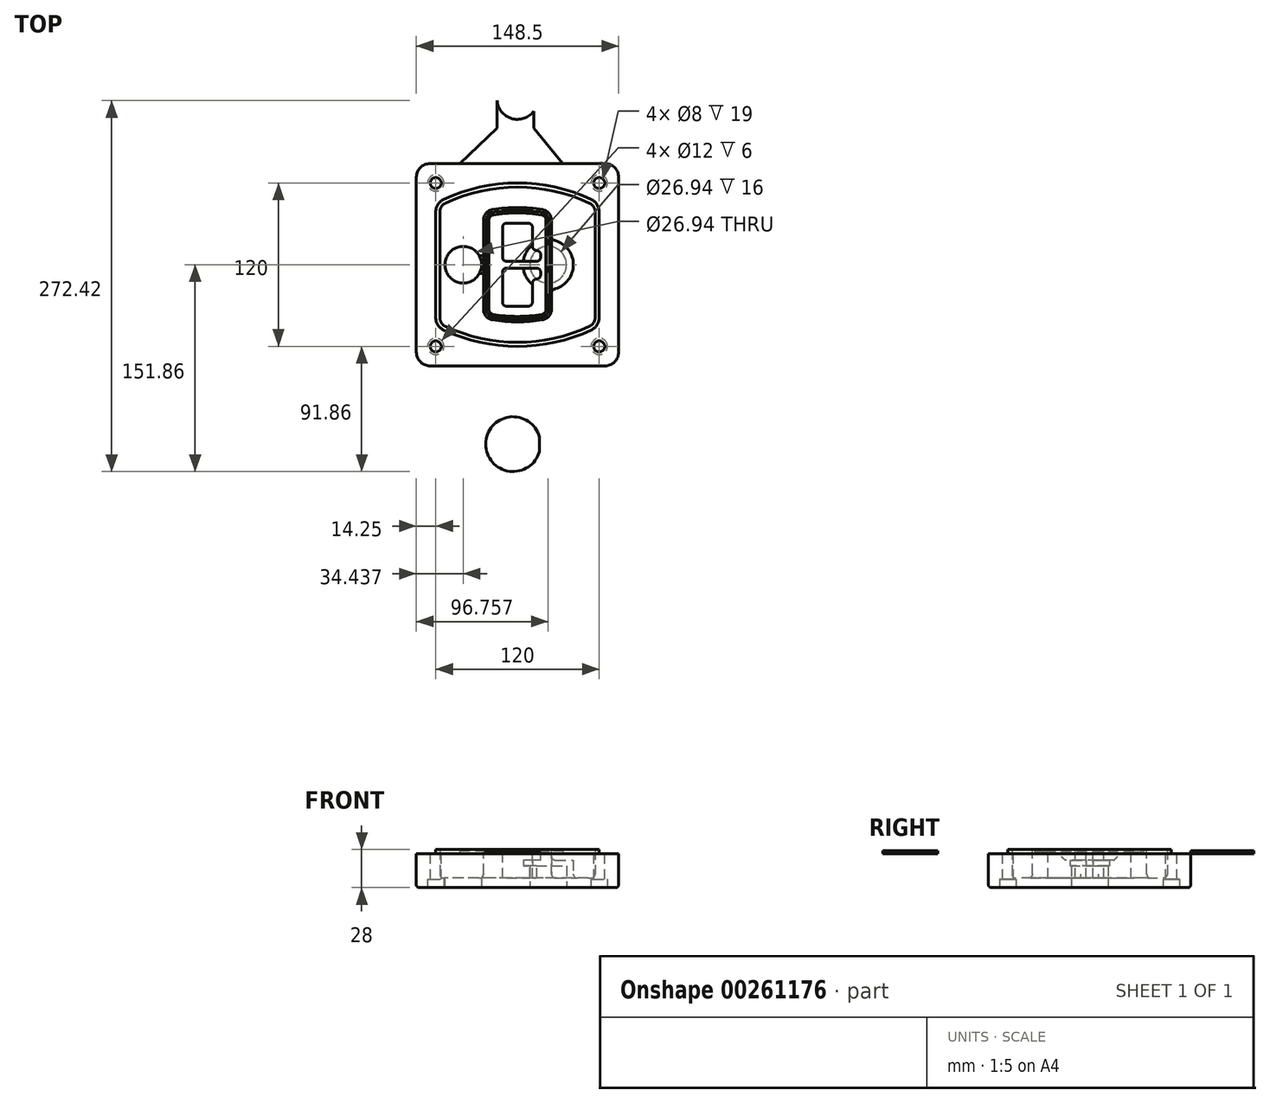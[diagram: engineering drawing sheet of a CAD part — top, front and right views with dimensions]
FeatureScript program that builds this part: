
annotation { "Feature Type Name" : "Feature", "Feature Type Description" : "" }
export const myFeature = defineFeature(function(context is Context, id is Id, definition is map)
    precondition{}
    {
        {
            var Q0;
            Q0=qCreatedBy(makeId("Top.planeOp"),FACE);
            var sketch = newSketch(context, id + "F0", { "sketchPlane" : qUnion([Q0])});
            skPoint(sketch, "E0.rect.middle", {"position": v(0, 0) * mm});
            skLineSegment(sketch, "E1.bottom", {"start": v(-64.25, -74.25) * mm, "end": v(64.25, -74.25) * mm});
            skLineSegment(sketch, "E1.top", {"start": v(-64.25, 74.25) * mm, "end": v(64.25, 74.25) * mm});
            skLineSegment(sketch, "E1.left", {"start": v(-74.25, -64.25) * mm, "end": v(-74.25, 64.25) * mm});
            skLineSegment(sketch, "E1.right", {"start": v(74.25, -64.25) * mm, "end": v(74.25, 64.25) * mm});
            skLineSegment(sketch, "E2", {"start": v(-74.25, 74.25) * mm, "end": v(74.25, -74.25) * mm, "construction": true});
            skLineSegment(sketch, "E3", {"start": v(74.25, 74.25) * mm, "end": v(-74.25, -74.25) * mm, "construction": true});
            skCircle(sketch, "E4", {"center": v(-60, 60) * mm, "radius": 4 * mm});
            skCircle(sketch, "E5", {"center": v(60, 60) * mm, "radius": 4 * mm});
            skCircle(sketch, "E6", {"center": v(60, -60) * mm, "radius": 4 * mm});
            skCircle(sketch, "E7", {"center": v(-60, -60) * mm, "radius": 4 * mm});
            skLineSegment(sketch, "E8", {"start": v(-60, 60) * mm, "end": v(60, 60) * mm, "construction": true});
            skLineSegment(sketch, "E9", {"start": v(60, 60) * mm, "end": v(60, -60) * mm, "construction": true});
            skLineSegment(sketch, "E10", {"start": v(60, -60) * mm, "end": v(-60, -60) * mm, "construction": true});
            skLineSegment(sketch, "E11", {"start": v(-60, -60) * mm, "end": v(-60, 60) * mm, "construction": true});
            skLineSegment(sketch, "E12", {"start": v(-60, 38.83) * mm, "end": v(-60, -38.83) * mm});
            skLineSegment(sketch, "E13", {"start": v(60, 38.83) * mm, "end": v(60, -38.83) * mm});
            skArc(sketch, "E14", {"start": v(54.26, 47.88) * mm, "mid": v(0, 60) * mm, "end": v(-54.26, 47.88) * mm});
            skArc(sketch, "E15", {"start": v(-54.26, -47.88) * mm, "mid": v(0, -60) * mm, "end": v(54.26, -47.88) * mm});
            skLineSegment(sketch, "E16", {"start": v(-60, 0) * mm, "end": v(60, 0) * mm, "construction": true});
            skPoint(sketch, "E17.visualSharp", {"position": v(-60, -45) * mm});
            skArc(sketch, "E17.filletArc", {"start": v(-60, -38.83) * mm, "mid": v(-58.44, -44.2) * mm, "end": v(-54.26, -47.88) * mm});
            skPoint(sketch, "E18.visualSharp", {"position": v(-60, 45) * mm});
            skArc(sketch, "E18.filletArc", {"start": v(-54.26, 47.88) * mm, "mid": v(-58.44, 44.2) * mm, "end": v(-60, 38.83) * mm});
            skPoint(sketch, "E19.visualSharp", {"position": v(60, 45) * mm});
            skArc(sketch, "E19.filletArc", {"start": v(60, 38.83) * mm, "mid": v(58.44, 44.2) * mm, "end": v(54.26, 47.88) * mm});
            skPoint(sketch, "E20.visualSharp", {"position": v(60, -45) * mm});
            skArc(sketch, "E20.filletArc", {"start": v(54.26, -47.88) * mm, "mid": v(58.44, -44.2) * mm, "end": v(60, -38.83) * mm});
            skPoint(sketch, "E21.visualSharp", {"position": v(-74.25, 74.25) * mm});
            skArc(sketch, "E21.filletArc", {"start": v(-64.25, 74.25) * mm, "mid": v(-71.32, 71.32) * mm, "end": v(-74.25, 64.25) * mm});
            skPoint(sketch, "E22.visualSharp", {"position": v(74.25, 74.25) * mm});
            skArc(sketch, "E22.filletArc", {"start": v(74.25, 64.25) * mm, "mid": v(71.32, 71.32) * mm, "end": v(64.25, 74.25) * mm});
            skPoint(sketch, "E23.visualSharp", {"position": v(74.25, -74.25) * mm});
            skArc(sketch, "E23.filletArc", {"start": v(64.25, -74.25) * mm, "mid": v(71.32, -71.32) * mm, "end": v(74.25, -64.25) * mm});
            skPoint(sketch, "E24.visualSharp", {"position": v(-74.25, -74.25) * mm});
            skArc(sketch, "E24.filletArc", {"start": v(-74.25, -64.25) * mm, "mid": v(-71.32, -71.32) * mm, "end": v(-64.25, -74.25) * mm});
            skArc(sketch, "E25.0", {"start": v(57, 38.83) * mm, "mid": v(55.9, 42.58) * mm, "end": v(52.98, 45.17) * mm});
            skLineSegment(sketch, "E25.1", {"start": v(57, 38.83) * mm, "end": v(57, -38.83) * mm});
            skArc(sketch, "E25.2", {"start": v(52.98, -45.17) * mm, "mid": v(55.9, -42.58) * mm, "end": v(57, -38.83) * mm});
            skArc(sketch, "E25.3", {"start": v(-52.98, -45.17) * mm, "mid": v(0, -57) * mm, "end": v(52.98, -45.17) * mm});
            skArc(sketch, "E25.4", {"start": v(-57, -38.83) * mm, "mid": v(-55.9, -42.58) * mm, "end": v(-52.98, -45.17) * mm});
            skArc(sketch, "E25.5", {"start": v(52.98, 45.17) * mm, "mid": v(0, 57) * mm, "end": v(-52.98, 45.17) * mm});
            skLineSegment(sketch, "E25.6", {"start": v(-57, 38.83) * mm, "end": v(-57, -38.83) * mm});
            skArc(sketch, "E25.7", {"start": v(-52.98, 45.17) * mm, "mid": v(-55.9, 42.58) * mm, "end": v(-57, 38.83) * mm});
            skArc(sketch, "E26.0", {"start": v(-55.96, 51.5) * mm, "mid": v(-61.82, 46.33) * mm, "end": v(-64, 38.83) * mm});
            skArc(sketch, "E26.1", {"start": v(55.96, 51.5) * mm, "mid": v(0, 64) * mm, "end": v(-55.96, 51.5) * mm});
            skArc(sketch, "E26.2", {"start": v(64, 38.83) * mm, "mid": v(61.82, 46.33) * mm, "end": v(55.96, 51.5) * mm});
            skLineSegment(sketch, "E26.3", {"start": v(64, 38.83) * mm, "end": v(64, -38.83) * mm});
            skArc(sketch, "E26.4", {"start": v(55.96, -51.5) * mm, "mid": v(61.82, -46.33) * mm, "end": v(64, -38.83) * mm});
            skLineSegment(sketch, "E26.5", {"start": v(-64, 38.83) * mm, "end": v(-64, -38.83) * mm});
            skArc(sketch, "E26.6", {"start": v(-55.96, -51.5) * mm, "mid": v(0, -64) * mm, "end": v(55.96, -51.5) * mm});
            skArc(sketch, "E26.7", {"start": v(-64, -38.83) * mm, "mid": v(-61.82, -46.33) * mm, "end": v(-55.96, -51.5) * mm});
            skSolve(sketch);
        }
        {
            var Q0;
            Q0=makeQuery(id+"F0.imprint","IMPRINT",FACE,{"disambiguationData":[TD([[makeQuery(id+"F0.imprint","IMPRINT",EDGE,{"derivedFrom":sQuery(id+"F0.wireOp",EDGE,"E1.bottom")}),1.0]])]});
            var Q1;
            Q1=makeQuery(id+"F0.imprint","IMPRINT",FACE,{"disambiguationData":[TD([[makeQuery(id+"F0.imprint","IMPRINT",EDGE,{"derivedFrom":sQuery(id+"F0.wireOp",EDGE,"E12")}),1.0]])]});
            var Q2;
            Q2=makeQuery(id+"F0.imprint","IMPRINT",FACE,{"disambiguationData":[TD([[makeQuery(id+"F0.imprint","IMPRINT",EDGE,{"derivedFrom":sQuery(id+"F0.wireOp",EDGE,"E25.0")}),1.0]])]});
            var Q3;
            Q3=makeQuery(id+"F0.imprint","IMPRINT",FACE,{"disambiguationData":[TD([[makeQuery(id+"F0.imprint","IMPRINT",EDGE,{"derivedFrom":sQuery(id+"F0.wireOp",EDGE,"E12")}),-1.0]])]});
            extrude(context, id + "F1", {"entities" : qUnion([Q0, Q1, Q2, Q3]), "oppositeDirection" : true, "depth" : 25 * mm});
        }
        {
            var Q0;
            Q0=makeQuery(id+"F0.imprint","IMPRINT",FACE,{"disambiguationData":[TD([[makeQuery(id+"F0.imprint","IMPRINT",EDGE,{"derivedFrom":sQuery(id+"F0.wireOp",EDGE,"E12")}),1.0]])]});
            extrude(context, id + "F2", {"entities" : qUnion([Q0]), "operationType" : NewBodyOperationType.ADD, "depth" : 3 * mm});
        }
        {
            var Q0;
            Q0=makeQuery(id+"F0.imprint","IMPRINT",FACE,{"disambiguationData":[TD([[makeQuery(id+"F0.imprint","IMPRINT",EDGE,{"derivedFrom":sQuery(id+"F0.wireOp",EDGE,"E25.0")}),1.0]])]});
            extrude(context, id + "F3", {"entities" : qUnion([Q0]), "operationType" : NewBodyOperationType.REMOVE, "oppositeDirection" : true, "depth" : 18 * mm});
        }
        {
            var Q0;
            Q0=makeQuery(id+"F2.opExtrude","CAP_FACE",FACE,{"disambiguationData":[OSD([sQuery(id+"F0.wireOp",EDGE,"E12"),sQuery(id+"F0.wireOp",EDGE,"E13"),sQuery(id+"F0.wireOp",EDGE,"E14"),sQuery(id+"F0.wireOp",EDGE,"E15"),sQuery(id+"F0.wireOp",EDGE,"E17.filletArc"),sQuery(id+"F0.wireOp",EDGE,"E18.filletArc"),sQuery(id+"F0.wireOp",EDGE,"E19.filletArc"),sQuery(id+"F0.wireOp",EDGE,"E20.filletArc"),sQuery(id+"F0.wireOp",EDGE,"E25.0"),sQuery(id+"F0.wireOp",EDGE,"E25.1"),sQuery(id+"F0.wireOp",EDGE,"E25.2"),sQuery(id+"F0.wireOp",EDGE,"E25.3"),sQuery(id+"F0.wireOp",EDGE,"E25.4"),sQuery(id+"F0.wireOp",EDGE,"E25.5"),sQuery(id+"F0.wireOp",EDGE,"E25.6"),sQuery(id+"F0.wireOp",EDGE,"E25.7")])],"isStart":false});
            var sketch = newSketch(context, id + "F4", { "sketchPlane" : qUnion([Q0])});
            skArc(sketch, "E27.0", {"start": v(-18.34, -40.45) * mm, "mid": v(0, -42) * mm, "end": v(18.34, -40.45) * mm});
            skArc(sketch, "E28.0", {"start": v(18.34, 40.45) * mm, "mid": v(0, 42) * mm, "end": v(-18.34, 40.45) * mm});
            skLineSegment(sketch, "E29", {"start": v(-25, 32.57) * mm, "end": v(-25, -32.57) * mm});
            skLineSegment(sketch, "E30", {"start": v(25, 32.57) * mm, "end": v(25, -32.57) * mm});
            skLineSegment(sketch, "E31", {"start": v(-25, 39.1) * mm, "end": v(25, 39.1) * mm, "construction": true});
            skLineSegment(sketch, "E32", {"start": v(-25, -39.1) * mm, "end": v(25, -39.1) * mm, "construction": true});
            skPoint(sketch, "E33.visualSharp", {"position": v(-25, 39.1) * mm});
            skArc(sketch, "E33.filletArc", {"start": v(-18.34, 40.45) * mm, "mid": v(-23.11, 37.73) * mm, "end": v(-25, 32.57) * mm});
            skPoint(sketch, "E34.visualSharp", {"position": v(25, 39.1) * mm});
            skArc(sketch, "E34.filletArc", {"start": v(25, 32.57) * mm, "mid": v(23.11, 37.73) * mm, "end": v(18.34, 40.45) * mm});
            skPoint(sketch, "E35.visualSharp", {"position": v(25, -39.1) * mm});
            skArc(sketch, "E35.filletArc", {"start": v(18.34, -40.45) * mm, "mid": v(23.11, -37.73) * mm, "end": v(25, -32.57) * mm});
            skPoint(sketch, "E36.visualSharp", {"position": v(-25, -39.1) * mm});
            skArc(sketch, "E36.filletArc", {"start": v(-25, -32.57) * mm, "mid": v(-23.11, -37.73) * mm, "end": v(-18.34, -40.45) * mm});
            skArc(sketch, "E37.0", {"start": v(52.98, 45.17) * mm, "mid": v(0, 57) * mm, "end": v(-52.98, 45.17) * mm});
            skArc(sketch, "E37.1", {"start": v(-52.98, 45.17) * mm, "mid": v(-55.9, 42.58) * mm, "end": v(-57, 38.83) * mm});
            skLineSegment(sketch, "E37.2", {"start": v(-57, 38.83) * mm, "end": v(-57, -38.83) * mm});
            skArc(sketch, "E37.3", {"start": v(-57, -38.83) * mm, "mid": v(-55.9, -42.58) * mm, "end": v(-52.98, -45.17) * mm});
            skArc(sketch, "E37.4", {"start": v(-52.98, -45.17) * mm, "mid": v(0, -57) * mm, "end": v(52.98, -45.17) * mm});
            skArc(sketch, "E37.5", {"start": v(52.98, -45.17) * mm, "mid": v(55.9, -42.58) * mm, "end": v(57, -38.83) * mm});
            skLineSegment(sketch, "E37.6", {"start": v(57, 38.83) * mm, "end": v(57, -38.83) * mm});
            skArc(sketch, "E37.7", {"start": v(57, 38.83) * mm, "mid": v(55.9, 42.58) * mm, "end": v(52.98, 45.17) * mm});
            skLineSegment(sketch, "E38.0", {"start": v(23, 32.57) * mm, "end": v(23, -32.57) * mm});
            skArc(sketch, "E38.1", {"start": v(18, -38.48) * mm, "mid": v(21.58, -36.44) * mm, "end": v(23, -32.57) * mm});
            skArc(sketch, "E38.2", {"start": v(-18, -38.48) * mm, "mid": v(0, -40) * mm, "end": v(18, -38.48) * mm});
            skArc(sketch, "E38.3", {"start": v(-23, -32.57) * mm, "mid": v(-21.58, -36.44) * mm, "end": v(-18, -38.48) * mm});
            skLineSegment(sketch, "E38.4", {"start": v(-23, 32.57) * mm, "end": v(-23, -32.57) * mm});
            skArc(sketch, "E38.5", {"start": v(23, 32.57) * mm, "mid": v(21.58, 36.44) * mm, "end": v(18, 38.48) * mm});
            skArc(sketch, "E38.6", {"start": v(-18, 38.48) * mm, "mid": v(-21.58, 36.44) * mm, "end": v(-23, 32.57) * mm});
            skArc(sketch, "E38.7", {"start": v(18, 38.48) * mm, "mid": v(0, 40) * mm, "end": v(-18, 38.48) * mm});
            skArc(sketch, "E39.0", {"start": v(21, 32.57) * mm, "mid": v(20.06, 35.15) * mm, "end": v(17.67, 36.5) * mm});
            skLineSegment(sketch, "E39.1", {"start": v(21, 32.57) * mm, "end": v(21, -32.57) * mm});
            skArc(sketch, "E39.2", {"start": v(17.67, -36.5) * mm, "mid": v(20.06, -35.15) * mm, "end": v(21, -32.57) * mm});
            skArc(sketch, "E39.3", {"start": v(-17.67, -36.5) * mm, "mid": v(0, -38) * mm, "end": v(17.67, -36.5) * mm});
            skArc(sketch, "E39.4", {"start": v(-21, -32.57) * mm, "mid": v(-20.06, -35.15) * mm, "end": v(-17.67, -36.5) * mm});
            skArc(sketch, "E39.5", {"start": v(17.67, 36.5) * mm, "mid": v(0, 38) * mm, "end": v(-17.67, 36.5) * mm});
            skLineSegment(sketch, "E39.6", {"start": v(-21, 32.57) * mm, "end": v(-21, -32.57) * mm});
            skArc(sketch, "E39.7", {"start": v(-17.67, 36.5) * mm, "mid": v(-20.06, 35.15) * mm, "end": v(-21, 32.57) * mm});
            skLineSegment(sketch, "E40", {"start": v(-25, 0) * mm, "end": v(25, 0) * mm, "construction": true});
            skLineSegment(sketch, "E41", {"start": v(-11, 5.5) * mm, "end": v(-11, 27.5) * mm});
            skLineSegment(sketch, "E42", {"start": v(-8, 30.5) * mm, "end": v(8, 30.5) * mm});
            skLineSegment(sketch, "E43", {"start": v(11, 27.5) * mm, "end": v(11, 13.5) * mm});
            skLineSegment(sketch, "E44", {"start": v(14, 10.5) * mm, "end": v(14, 10.5) * mm});
            skLineSegment(sketch, "E45", {"start": v(17, 7.5) * mm, "end": v(17, 5.5) * mm});
            skLineSegment(sketch, "E46", {"start": v(14, 2.5) * mm, "end": v(-8, 2.5) * mm});
            skPoint(sketch, "E47.visualSharp", {"position": v(-11, 30.5) * mm});
            skArc(sketch, "E47.filletArc", {"start": v(-8, 30.5) * mm, "mid": v(-10.12, 29.62) * mm, "end": v(-11, 27.5) * mm});
            skPoint(sketch, "E48.visualSharp", {"position": v(11, 30.5) * mm});
            skArc(sketch, "E48.filletArc", {"start": v(11, 27.5) * mm, "mid": v(10.12, 29.62) * mm, "end": v(8, 30.5) * mm});
            skPoint(sketch, "E49.visualSharp", {"position": v(11, 10.5) * mm});
            skArc(sketch, "E49.filletArc", {"start": v(11, 13.5) * mm, "mid": v(11.88, 11.38) * mm, "end": v(14, 10.5) * mm});
            skPoint(sketch, "E50.visualSharp", {"position": v(17, 10.5) * mm});
            skArc(sketch, "E50.filletArc", {"start": v(17, 7.5) * mm, "mid": v(16.12, 9.62) * mm, "end": v(14, 10.5) * mm});
            skPoint(sketch, "E51.visualSharp", {"position": v(17, 2.5) * mm});
            skArc(sketch, "E51.filletArc", {"start": v(14, 2.5) * mm, "mid": v(16.12, 3.38) * mm, "end": v(17, 5.5) * mm});
            skPoint(sketch, "E52.visualSharp", {"position": v(-11, 2.5) * mm});
            skArc(sketch, "E52.filletArc", {"start": v(-11, 5.5) * mm, "mid": v(-10.12, 3.38) * mm, "end": v(-8, 2.5) * mm});
            skLineSegment(sketch, "E53.0.MirrorCS", {"start": v(14, -2.5) * mm, "end": v(-8, -2.5) * mm});
            skArc(sketch, "E54.0.MirrorCS", {"start": v(-11, -5.5) * mm, "mid": v(-10.12, -3.38) * mm, "end": v(-8, -2.5) * mm});
            skLineSegment(sketch, "E55.0.MirrorCS", {"start": v(-11, -5.5) * mm, "end": v(-11, -27.5) * mm});
            skArc(sketch, "E56.0.MirrorCS", {"start": v(-8, -30.5) * mm, "mid": v(-10.12, -29.62) * mm, "end": v(-11, -27.5) * mm});
            skLineSegment(sketch, "E57.0.MirrorCS", {"start": v(-8, -30.5) * mm, "end": v(8, -30.5) * mm});
            skArc(sketch, "E58.0.MirrorCS", {"start": v(11, -27.5) * mm, "mid": v(10.12, -29.62) * mm, "end": v(8, -30.5) * mm});
            skLineSegment(sketch, "E59.0.MirrorCS", {"start": v(11, -27.5) * mm, "end": v(11, -13.5) * mm});
            skArc(sketch, "E60.0.MirrorCS", {"start": v(11, -13.5) * mm, "mid": v(11.88, -11.38) * mm, "end": v(14, -10.5) * mm});
            skArc(sketch, "E61.0.MirrorCS", {"start": v(17, -7.5) * mm, "mid": v(16.12, -9.62) * mm, "end": v(14, -10.5) * mm});
            skLineSegment(sketch, "E62.0.MirrorCS", {"start": v(17, -7.5) * mm, "end": v(17, -5.5) * mm});
            skArc(sketch, "E63.0.MirrorCS", {"start": v(14, -2.5) * mm, "mid": v(16.12, -3.38) * mm, "end": v(17, -5.5) * mm});
            skSolve(sketch);
        }
        {
            var Q0;
            Q0=makeQuery(id+"F4.imprint","IMPRINT",FACE,{"disambiguationData":[TD([[makeQuery(id+"F4.imprint","IMPRINT",EDGE,{"derivedFrom":sQuery(id+"F4.wireOp",EDGE,"E27.0")}),1.0]])]});
            var Q1;
            Q1=makeQuery(id+"F4.imprint","IMPRINT",FACE,{"disambiguationData":[TD([[makeQuery(id+"F4.imprint","IMPRINT",EDGE,{"derivedFrom":sQuery(id+"F4.wireOp",EDGE,"E38.0")}),-1.0]])]});
            var Q2;
            Q2=makeQuery(id+"F4.imprint","IMPRINT",FACE,{"disambiguationData":[TD([[makeQuery(id+"F4.imprint","IMPRINT",EDGE,{"derivedFrom":sQuery(id+"F4.wireOp",EDGE,"E39.0")}),1.0]])]});
            extrude(context, id + "F5", {"entities" : qUnion([Q0, Q1, Q2]), "operationType" : NewBodyOperationType.ADD, "endBound" : BoundingType.UP_TO_NEXT, "oppositeDirection" : true, "depth" : 25 * mm});
        }
        {
            var Q0;
            Q0=makeQuery(id+"F4.imprint","IMPRINT",FACE,{"disambiguationData":[TD([[makeQuery(id+"F4.imprint","IMPRINT",EDGE,{"derivedFrom":sQuery(id+"F4.wireOp",EDGE,"E38.0")}),-1.0]])]});
            extrude(context, id + "F6", {"entities" : qUnion([Q0]), "operationType" : NewBodyOperationType.REMOVE, "oppositeDirection" : true, "depth" : 2 * mm});
        }
        {
            var Q0;
            Q0=makeQuery(id+"F1.opExtrude","CAP_FACE",FACE,{"disambiguationData":[OSD([sQuery(id+"F0.wireOp",EDGE,"E1.bottom"),sQuery(id+"F0.wireOp",EDGE,"E1.top"),sQuery(id+"F0.wireOp",EDGE,"E1.left"),sQuery(id+"F0.wireOp",EDGE,"E1.right"),sQuery(id+"F0.wireOp",EDGE,"E4"),sQuery(id+"F0.wireOp",EDGE,"E5"),sQuery(id+"F0.wireOp",EDGE,"E6"),sQuery(id+"F0.wireOp",EDGE,"E7"),sQuery(id+"F0.wireOp",EDGE,"E21.filletArc"),sQuery(id+"F0.wireOp",EDGE,"E22.filletArc"),sQuery(id+"F0.wireOp",EDGE,"E23.filletArc"),sQuery(id+"F0.wireOp",EDGE,"E24.filletArc")])],"isStart":false});
            var sketch = newSketch(context, id + "F7", { "sketchPlane" : qUnion([Q0])});
            skCircle(sketch, "E64", {"center": v(22.5, 0) * mm, "radius": 13.47 * mm});
            skCircle(sketch, "E65", {"center": v(-39.81, 0) * mm, "radius": 13.47 * mm});
            skLineSegment(sketch, "E66", {"start": v(74.25, 0) * mm, "end": v(-74.25, 0) * mm});
            skCircle(sketch, "E67", {"center": v(22.5, 0) * mm, "radius": 18.47 * mm});
            skCircle(sketch, "E68", {"center": v(60, -60) * mm, "radius": 6 * mm});
            skCircle(sketch, "E69", {"center": v(-60, -60) * mm, "radius": 6 * mm});
            skCircle(sketch, "E70", {"center": v(-60, 60) * mm, "radius": 6 * mm});
            skCircle(sketch, "E71", {"center": v(60, 60) * mm, "radius": 6 * mm});
            skSolve(sketch);
        }
        {
            var Q0;
            {var subQ1=sQuery(id+"F7.wireOp",EDGE,"E66");var subQ4=sQuery(id+"F7.wireOp",EDGE,"E64");var subQ6=makeQuery(id+"F7.imprint","INTERSECT",VERTEX,{"disambiguationData":[OD(0.0)],"derivedFrom":[subQ4,subQ1]});Q0=makeQuery(id+"F7.imprint","IMPRINT",FACE,{"disambiguationData":[TD([[makeQuery(id+"F7.imprint","IMPRINT",EDGE,{"disambiguationData":[TD([[subQ6,-1.0]])],"derivedFrom":subQ4}),-1.0]])]});}
            var Q1;
            {var subQ0=sQuery(id+"F7.wireOp",EDGE,"E66");var subQ1=sQuery(id+"F7.wireOp",EDGE,"E64");var subQ3=makeQuery(id+"F7.imprint","INTERSECT",VERTEX,{"disambiguationData":[OD(0.0)],"derivedFrom":[subQ1,subQ0]});Q1=makeQuery(id+"F7.imprint","IMPRINT",FACE,{"disambiguationData":[TD([[makeQuery(id+"F7.imprint","IMPRINT",EDGE,{"disambiguationData":[TD([[subQ3,-1.0]])],"derivedFrom":subQ1}),1.0]])]});}
            var Q2;
            {var subQ0=sQuery(id+"F7.wireOp",EDGE,"E66");var subQ1=sQuery(id+"F7.wireOp",EDGE,"E64");var subQ3=makeQuery(id+"F7.imprint","INTERSECT",VERTEX,{"disambiguationData":[OD(0.0)],"derivedFrom":[subQ1,subQ0]});Q2=makeQuery(id+"F7.imprint","IMPRINT",FACE,{"disambiguationData":[TD([[makeQuery(id+"F7.imprint","IMPRINT",EDGE,{"disambiguationData":[TD([[subQ3,1.0]])],"derivedFrom":subQ1}),1.0]])]});}
            var Q3;
            {var subQ1=sQuery(id+"F7.wireOp",EDGE,"E66");var subQ4=sQuery(id+"F7.wireOp",EDGE,"E64");var subQ6=makeQuery(id+"F7.imprint","INTERSECT",VERTEX,{"disambiguationData":[OD(0.0)],"derivedFrom":[subQ4,subQ1]});Q3=makeQuery(id+"F7.imprint","IMPRINT",FACE,{"disambiguationData":[TD([[makeQuery(id+"F7.imprint","IMPRINT",EDGE,{"disambiguationData":[TD([[subQ6,1.0]])],"derivedFrom":subQ4}),-1.0]])]});}
            extrude(context, id + "F8", {"entities" : qUnion([Q0, Q1, Q2, Q3]), "operationType" : NewBodyOperationType.ADD, "oppositeDirection" : true, "depth" : 20 * mm});
        }
        {
            var Q0;
            {var subQ0=sQuery(id+"F7.wireOp",EDGE,"E66");var subQ1=sQuery(id+"F7.wireOp",EDGE,"E64");var subQ3=makeQuery(id+"F7.imprint","INTERSECT",VERTEX,{"disambiguationData":[OD(0.0)],"derivedFrom":[subQ1,subQ0]});Q0=makeQuery(id+"F7.imprint","IMPRINT",FACE,{"disambiguationData":[TD([[makeQuery(id+"F7.imprint","IMPRINT",EDGE,{"disambiguationData":[TD([[subQ3,-1.0]])],"derivedFrom":subQ1}),1.0]])]});}
            var Q1;
            {var subQ0=sQuery(id+"F7.wireOp",EDGE,"E66");var subQ1=sQuery(id+"F7.wireOp",EDGE,"E64");var subQ3=makeQuery(id+"F7.imprint","INTERSECT",VERTEX,{"disambiguationData":[OD(0.0)],"derivedFrom":[subQ1,subQ0]});Q1=makeQuery(id+"F7.imprint","IMPRINT",FACE,{"disambiguationData":[TD([[makeQuery(id+"F7.imprint","IMPRINT",EDGE,{"disambiguationData":[TD([[subQ3,1.0]])],"derivedFrom":subQ1}),1.0]])]});}
            extrude(context, id + "F9", {"entities" : qUnion([Q0, Q1]), "operationType" : NewBodyOperationType.REMOVE, "oppositeDirection" : true, "depth" : 16 * mm});
        }
        {
            var Q0;
            {var subQ0=sQuery(id+"F7.wireOp",EDGE,"E66");var subQ1=sQuery(id+"F7.wireOp",EDGE,"E65");var subQ3=makeQuery(id+"F7.imprint","INTERSECT",VERTEX,{"disambiguationData":[OD(0.0)],"derivedFrom":[subQ1,subQ0]});Q0=makeQuery(id+"F7.imprint","IMPRINT",FACE,{"disambiguationData":[TD([[makeQuery(id+"F7.imprint","IMPRINT",EDGE,{"disambiguationData":[TD([[subQ3,-1.0]])],"derivedFrom":subQ1}),1.0]])]});}
            var Q1;
            {var subQ0=sQuery(id+"F7.wireOp",EDGE,"E66");var subQ1=sQuery(id+"F7.wireOp",EDGE,"E65");var subQ3=makeQuery(id+"F7.imprint","INTERSECT",VERTEX,{"disambiguationData":[OD(0.0)],"derivedFrom":[subQ1,subQ0]});Q1=makeQuery(id+"F7.imprint","IMPRINT",FACE,{"disambiguationData":[TD([[makeQuery(id+"F7.imprint","IMPRINT",EDGE,{"disambiguationData":[TD([[subQ3,1.0]])],"derivedFrom":subQ1}),1.0]])]});}
            extrude(context, id + "F10", {"entities" : qUnion([Q0, Q1]), "operationType" : NewBodyOperationType.REMOVE, "oppositeDirection" : true, "depth" : 25 * mm});
        }
        {
            var Q0;
            Q0=makeQuery(id+"F7.imprint","IMPRINT",FACE,{"disambiguationData":[TD([[makeQuery(id+"F7.imprint","IMPRINT",EDGE,{"derivedFrom":sQuery(id+"F7.wireOp",EDGE,"E68")}),1.0]])]});
            var Q1;
            Q1=makeQuery(id+"F7.imprint","IMPRINT",FACE,{"disambiguationData":[TD([[makeQuery(id+"F7.imprint","IMPRINT",EDGE,{"derivedFrom":makeQuery(id+"F1.opExtrude","CAP_EDGE",EDGE,{"disambiguationData":[OSD([sQuery(id+"F0.wireOp",EDGE,"E5")])],"isStart":false})}),-1.0]])]});
            var Q2;
            Q2=makeQuery(id+"F7.imprint","IMPRINT",FACE,{"disambiguationData":[TD([[makeQuery(id+"F7.imprint","IMPRINT",EDGE,{"derivedFrom":sQuery(id+"F7.wireOp",EDGE,"E69")}),1.0]])]});
            var Q3;
            Q3=makeQuery(id+"F7.imprint","IMPRINT",FACE,{"disambiguationData":[TD([[makeQuery(id+"F7.imprint","IMPRINT",EDGE,{"derivedFrom":makeQuery(id+"F1.opExtrude","CAP_EDGE",EDGE,{"disambiguationData":[OSD([sQuery(id+"F0.wireOp",EDGE,"E4")])],"isStart":false})}),-1.0]])]});
            var Q4;
            Q4=makeQuery(id+"F7.imprint","IMPRINT",FACE,{"disambiguationData":[TD([[makeQuery(id+"F7.imprint","IMPRINT",EDGE,{"derivedFrom":sQuery(id+"F7.wireOp",EDGE,"E70")}),1.0]])]});
            var Q5;
            Q5=makeQuery(id+"F7.imprint","IMPRINT",FACE,{"disambiguationData":[TD([[makeQuery(id+"F7.imprint","IMPRINT",EDGE,{"derivedFrom":makeQuery(id+"F1.opExtrude","CAP_EDGE",EDGE,{"disambiguationData":[OSD([sQuery(id+"F0.wireOp",EDGE,"E7")])],"isStart":false})}),-1.0]])]});
            var Q6;
            Q6=makeQuery(id+"F7.imprint","IMPRINT",FACE,{"disambiguationData":[TD([[makeQuery(id+"F7.imprint","IMPRINT",EDGE,{"derivedFrom":sQuery(id+"F7.wireOp",EDGE,"E71")}),1.0]])]});
            var Q7;
            Q7=makeQuery(id+"F7.imprint","IMPRINT",FACE,{"disambiguationData":[TD([[makeQuery(id+"F7.imprint","IMPRINT",EDGE,{"derivedFrom":makeQuery(id+"F1.opExtrude","CAP_EDGE",EDGE,{"disambiguationData":[OSD([sQuery(id+"F0.wireOp",EDGE,"E6")])],"isStart":false})}),-1.0]])]});
            extrude(context, id + "F11", {"entities" : qUnion([Q0, Q1, Q2, Q3, Q4, Q5, Q6, Q7]), "operationType" : NewBodyOperationType.REMOVE, "oppositeDirection" : true, "depth" : 6 * mm});
        }
        {
            var Q0;
            Q0=makeQuery(id+"F9.boolean.opBoolean","COPY",FACE,{"derivedFrom":makeQuery(id+"F9.opExtrude","CAP_FACE",FACE,{"disambiguationData":[OSD([sQuery(id+"F7.wireOp",EDGE,"E64")])],"isStart":false})});
            var sketch = newSketch(context, id + "F12", { "sketchPlane" : qUnion([Q0])});
            skArc(sketch, "E72.0", {"start": v(11, 14.45) * mm, "mid": v(6.45, 9.13) * mm, "end": v(4.2, 2.5) * mm});
            skArc(sketch, "E72.1", {"start": v(4.2, -2.5) * mm, "mid": v(6.45, -9.13) * mm, "end": v(11, -14.45) * mm});
            skLineSegment(sketch, "E73", {"start": v(4.2, -2.5) * mm, "end": v(14, -2.5) * mm});
            skLineSegment(sketch, "E74.0", {"start": v(14, 2.5) * mm, "end": v(4.2, 2.5) * mm});
            skArc(sketch, "E74.1", {"start": v(14, 2.5) * mm, "mid": v(16.12, 3.38) * mm, "end": v(17, 5.5) * mm});
            skLineSegment(sketch, "E74.2", {"start": v(17, 7.5) * mm, "end": v(17, 5.5) * mm});
            skArc(sketch, "E74.3", {"start": v(17, 7.5) * mm, "mid": v(16.12, 9.62) * mm, "end": v(14, 10.5) * mm});
            skArc(sketch, "E74.4", {"start": v(11, 13.5) * mm, "mid": v(11.88, 11.38) * mm, "end": v(14, 10.5) * mm});
            skLineSegment(sketch, "E74.5", {"start": v(11, 14.45) * mm, "end": v(11, 13.5) * mm});
            skLineSegment(sketch, "E74.7", {"start": v(14, -2.5) * mm, "end": v(4.2, -2.5) * mm});
            skArc(sketch, "E74.8", {"start": v(14, -2.5) * mm, "mid": v(16.12, -3.38) * mm, "end": v(17, -5.5) * mm});
            skLineSegment(sketch, "E74.9", {"start": v(17, -7.5) * mm, "end": v(17, -5.5) * mm});
            skArc(sketch, "E74.10", {"start": v(17, -7.5) * mm, "mid": v(16.12, -9.62) * mm, "end": v(14, -10.5) * mm});
            skArc(sketch, "E74.11", {"start": v(11, -13.5) * mm, "mid": v(11.88, -11.38) * mm, "end": v(14, -10.5) * mm});
            skLineSegment(sketch, "E74.12", {"start": v(11, -14.45) * mm, "end": v(11, -13.5) * mm});
            skPoint(sketch, "E75.orphan", {"position": v(11, -27.5) * mm});
            skPoint(sketch, "E76.orphan", {"position": v(-8, -2.5) * mm});
            skPoint(sketch, "E77.orphan", {"position": v(-8, 2.5) * mm});
            skPoint(sketch, "E78.orphan", {"position": v(11, 27.5) * mm});
            skSolve(sketch);
        }
        {
            var Q0;
            {var subQ7=sQuery(id+"F12.wireOp",EDGE,"E72.0");var subQ14=sQuery(id+"F12.wireOp",EDGE,"E72.1");var subQ16=sQuery(id+"F12.wireOp",EDGE,"E74.1");var subQ18=sQuery(id+"F12.wireOp",EDGE,"E74.8");Q0=qUnion([makeQuery(id+"F12.imprint","IMPRINT",FACE,{"disambiguationData":[TD([[makeQuery(id+"F12.imprint","IMPRINT",EDGE,{"derivedFrom":subQ7}),1.0]])]}),makeQuery(id+"F12.imprint","IMPRINT",FACE,{"disambiguationData":[TD([[makeQuery(id+"F12.imprint","IMPRINT",EDGE,{"derivedFrom":subQ14}),1.0]])]}),makeQuery(id+"F12.imprint","IMPRINT",FACE,{"disambiguationData":[TD([[makeQuery(id+"F12.imprint","IMPRINT",EDGE,{"derivedFrom":subQ16}),1.0]])]}),makeQuery(id+"F12.imprint","IMPRINT",FACE,{"disambiguationData":[TD([[makeQuery(id+"F12.imprint","IMPRINT",EDGE,{"derivedFrom":subQ18}),-1.0]])]})]);}
            var Q1;
            Q1=makeQuery(id+"F5.boolean.opBoolean","SPLIT",FACE,{"disambiguationData":[TD([makeQuery(id+"F5.opExtrude","SWEPT_FACE",FACE,{"disambiguationData":[OSD([sQuery(id+"F4.wireOp",EDGE,"E41")])]})])],"derivedFrom":makeQuery(id+"F3.boolean.opBoolean","COPY",FACE,{"derivedFrom":makeQuery(id+"F3.opExtrude","CAP_FACE",FACE,{"disambiguationData":[OSD([sQuery(id+"F0.wireOp",EDGE,"E25.0"),sQuery(id+"F0.wireOp",EDGE,"E25.1"),sQuery(id+"F0.wireOp",EDGE,"E25.2"),sQuery(id+"F0.wireOp",EDGE,"E25.3"),sQuery(id+"F0.wireOp",EDGE,"E25.4"),sQuery(id+"F0.wireOp",EDGE,"E25.5"),sQuery(id+"F0.wireOp",EDGE,"E25.6"),sQuery(id+"F0.wireOp",EDGE,"E25.7")])],"isStart":false})})});
            extrude(context, id + "F13", {"entities" : qUnion([Q0]), "operationType" : NewBodyOperationType.REMOVE, "endBound" : BoundingType.UP_TO_SURFACE, "endBoundEntityFace" : qUnion([Q1]), "depth" : 25 * mm});
        }
        {
            var Q0;
            Q0=makeQuery(id+"F3.boolean.opBoolean","COPY",EDGE,{"derivedFrom":makeQuery(id+"F3.opExtrude","CAP_EDGE",EDGE,{"disambiguationData":[OSD([sQuery(id+"F0.wireOp",EDGE,"E25.6")])],"isStart":false})});
            var Q1;
            Q1=makeQuery(id+"F8.boolean.opBoolean","INTERSECT",EDGE,{"derivedFrom":[makeQuery(id+"F5.opExtrude","SWEPT_FACE",FACE,{"disambiguationData":[OSD([sQuery(id+"F4.wireOp",EDGE,"E30")])]}),makeQuery(id+"F8.opExtrude","CAP_FACE",FACE,{"disambiguationData":[OSD([sQuery(id+"F7.wireOp",EDGE,"E67")])],"isStart":false})]});
            var Q2;
            Q2=makeQuery(id+"F8.boolean.opBoolean","INTERSECT",EDGE,{"disambiguationData":[OD(1.0)],"derivedFrom":[makeQuery(id+"F5.opExtrude","SWEPT_FACE",FACE,{"disambiguationData":[OSD([sQuery(id+"F4.wireOp",EDGE,"E30")])]}),makeQuery(id+"F8.opExtrude","SWEPT_FACE",FACE,{"disambiguationData":[OSD([sQuery(id+"F7.wireOp",EDGE,"E67")])]})]});
            var Q3;
            {var subQ0=sQuery(id+"F4.wireOp",EDGE,"E30");Q3=makeQuery(id+"F8.boolean.opBoolean","SPLIT",EDGE,{"disambiguationData":[TD([makeQuery(id+"F5.opExtrude","SWEPT_FACE",FACE,{"disambiguationData":[OSD([sQuery(id+"F4.wireOp",EDGE,"E35.filletArc")])]})])],"derivedFrom":makeQuery(id+"F5.opExtrude","CAP_EDGE",EDGE,{"disambiguationData":[OSD([subQ0])],"isStart":false})});}
            var Q4;
            {var subQ0=sQuery(id+"F0.wireOp",EDGE,"E25.7");var subQ1=sQuery(id+"F0.wireOp",EDGE,"E25.1");var subQ2=sQuery(id+"F0.wireOp",EDGE,"E25.6");var subQ3=sQuery(id+"F0.wireOp",EDGE,"E25.5");var subQ4=sQuery(id+"F0.wireOp",EDGE,"E25.4");var subQ5=sQuery(id+"F0.wireOp",EDGE,"E25.0");var subQ6=sQuery(id+"F0.wireOp",EDGE,"E25.2");var subQ7=sQuery(id+"F0.wireOp",EDGE,"E25.3");Q4=makeQuery(id+"F8.boolean.opBoolean","INTERSECT",EDGE,{"derivedFrom":[makeQuery(id+"F5.boolean.opBoolean","SPLIT",FACE,{"disambiguationData":[TD([makeQuery(id+"F2.opExtrude","SWEPT_FACE",FACE,{"disambiguationData":[OSD([subQ5])]})])],"derivedFrom":makeQuery(id+"F3.boolean.opBoolean","COPY",FACE,{"derivedFrom":makeQuery(id+"F3.opExtrude","CAP_FACE",FACE,{"disambiguationData":[OSD([subQ5,subQ1,subQ6,subQ7,subQ4,subQ3,subQ2,subQ0])],"isStart":false})})}),makeQuery(id+"F8.opExtrude","SWEPT_FACE",FACE,{"disambiguationData":[OSD([sQuery(id+"F7.wireOp",EDGE,"E67")])]})]});}
            var Q5;
            Q5=makeQuery(id+"F8.boolean.opBoolean","INTERSECT",EDGE,{"disambiguationData":[OD(0.0)],"derivedFrom":[makeQuery(id+"F5.opExtrude","SWEPT_FACE",FACE,{"disambiguationData":[OSD([sQuery(id+"F4.wireOp",EDGE,"E30")])]}),makeQuery(id+"F8.opExtrude","SWEPT_FACE",FACE,{"disambiguationData":[OSD([sQuery(id+"F7.wireOp",EDGE,"E67")])]})]});
            fillet(context, id + "F14", {"entities" : qUnion([Q0, Q1, Q2, Q3, Q4, Q5]), "radius" : 3 * mm, "tangentPropagation" : true, "allowEdgeOverflow" : false});
        }
        {
            var Q0;
            Q0=makeQuery(id+"F1.opExtrude","CAP_EDGE",EDGE,{"disambiguationData":[OSD([sQuery(id+"F0.wireOp",EDGE,"E1.bottom")])],"isStart":false});
            fillet(context, id + "F15", {"entities" : qUnion([Q0]), "radius" : 2 * mm, "tangentPropagation" : true, "allowEdgeOverflow" : false});
        }
        {
            var Q0;
            {var subQ0=sQuery(id+"F0.wireOp",EDGE,"E22.filletArc");var subQ1=sQuery(id+"F0.wireOp",EDGE,"E7");var subQ2=sQuery(id+"F0.wireOp",EDGE,"E6");var subQ3=sQuery(id+"F0.wireOp",EDGE,"E5");var subQ4=sQuery(id+"F0.wireOp",EDGE,"E4");var subQ5=sQuery(id+"F0.wireOp",EDGE,"E1.bottom");var subQ6=sQuery(id+"F0.wireOp",EDGE,"E21.filletArc");var subQ7=sQuery(id+"F0.wireOp",EDGE,"E1.top");var subQ8=sQuery(id+"F0.wireOp",EDGE,"E1.left");var subQ9=sQuery(id+"F0.wireOp",EDGE,"E1.right");var subQ10=sQuery(id+"F0.wireOp",EDGE,"E23.filletArc");var subQ11=sQuery(id+"F0.wireOp",EDGE,"E24.filletArc");Q0=makeQuery(id+"F2.boolean.opBoolean","SPLIT",FACE,{"disambiguationData":[TD([makeQuery(id+"F1.opExtrude","SWEPT_FACE",FACE,{"disambiguationData":[OSD([subQ5])]})])],"derivedFrom":makeQuery(id+"F1.opExtrude","CAP_FACE",FACE,{"disambiguationData":[OSD([subQ5,subQ7,subQ8,subQ9,subQ4,subQ3,subQ2,subQ1,subQ6,subQ0,subQ10,subQ11])],"isStart":true})});}
            var sketch = newSketch(context, id + "F16", { "sketchPlane" : qUnion([Q0])});
            skLineSegment(sketch, "E79", {"start": v(0, 0) * mm, "end": v(0, 121.74) * mm, "construction": true});
            skLineSegment(sketch, "E80", {"start": v(-42.43, 74.25) * mm, "end": v(-14.95, 100.15) * mm});
            skLineSegment(sketch, "E81", {"start": v(-14.95, 100.15) * mm, "end": v(-14.95, 120.56) * mm});
            skLineSegment(sketch, "E82", {"start": v(33.23, 74.25) * mm, "end": v(11.87, 100.15) * mm});
            skLineSegment(sketch, "E83", {"start": v(11.87, 100.15) * mm, "end": v(11.87, 119.36) * mm});
            skArc(sketch, "E84", {"start": v(-14.95, 120.56) * mm, "mid": v(15, 121.74) * mm, "end": v(-14.95, 122.93) * mm});
            skSolve(sketch);
        }
        {
            var Q0;
            Q0=makeQuery(id+"F16.imprint","IMPRINT",FACE,{"disambiguationData":[TD([[makeQuery(id+"F16.imprint","IMPRINT",EDGE,{"derivedFrom":makeQuery(id+"F1.opExtrude","CAP_EDGE",EDGE,{"disambiguationData":[OSD([sQuery(id+"F0.wireOp",EDGE,"E1.bottom")])],"isStart":true})}),1.0]])]});
            var sketch = newSketch(context, id + "F18", { "sketchPlane" : qUnion([Q0])});
            skLineSegment(sketch, "E85", {"start": v(-37.26, -75.31) * mm, "end": v(-19.98, -111.9) * mm});
            skLineSegment(sketch, "E86", {"start": v(-19.98, -138.2) * mm, "end": v(-19.98, -111.9) * mm});
            skLineSegment(sketch, "E87", {"start": v(38.09, -75.32) * mm, "end": v(16.16, -111.64) * mm});
            skLineSegment(sketch, "E88", {"start": v(16.16, -111.64) * mm, "end": v(16.17, -137.07) * mm});
            skCircle(sketch, "E89", {"center": v(-3.22, -131.75) * mm, "radius": 20.11 * mm});
            skPoint(sketch, "E89.first.point", {"position": v(0, -151.6) * mm});
            skPoint(sketch, "E89.third.point", {"position": v(0, -111.9) * mm});
            skSolve(sketch);
        }
        {
            var Q0;
            {var subQ4=sQuery(id+"F16.wireOp",EDGE,"E80");Q0=makeQuery(id+"F16.imprint","IMPRINT",FACE,{"disambiguationData":[TD([[makeQuery(id+"F16.imprint","IMPRINT",EDGE,{"derivedFrom":subQ4}),-1.0]])]});}
            var Q1;
            {var subQ0=sQuery(id+"F18.wireOp",EDGE,"E89");var subQ1=sQuery(id+"F18.wireOp",EDGE,"E88");var subQ2=makeQuery(id+"F18.imprint","INTERSECT",VERTEX,{"disambiguationData":[OD(0.0)],"derivedFrom":[subQ1,subQ0]});Q1=makeQuery(id+"F18.imprint","IMPRINT",FACE,{"disambiguationData":[TD([[makeQuery(id+"F18.imprint","IMPRINT",EDGE,{"disambiguationData":[TD([[subQ2,1.0]])],"derivedFrom":subQ1}),-1.0]])]});}
            extrude(context, id + "F17", {"entities" : qUnion([Q0, Q1]), "depth" : 2 * mm});
        }
    });
